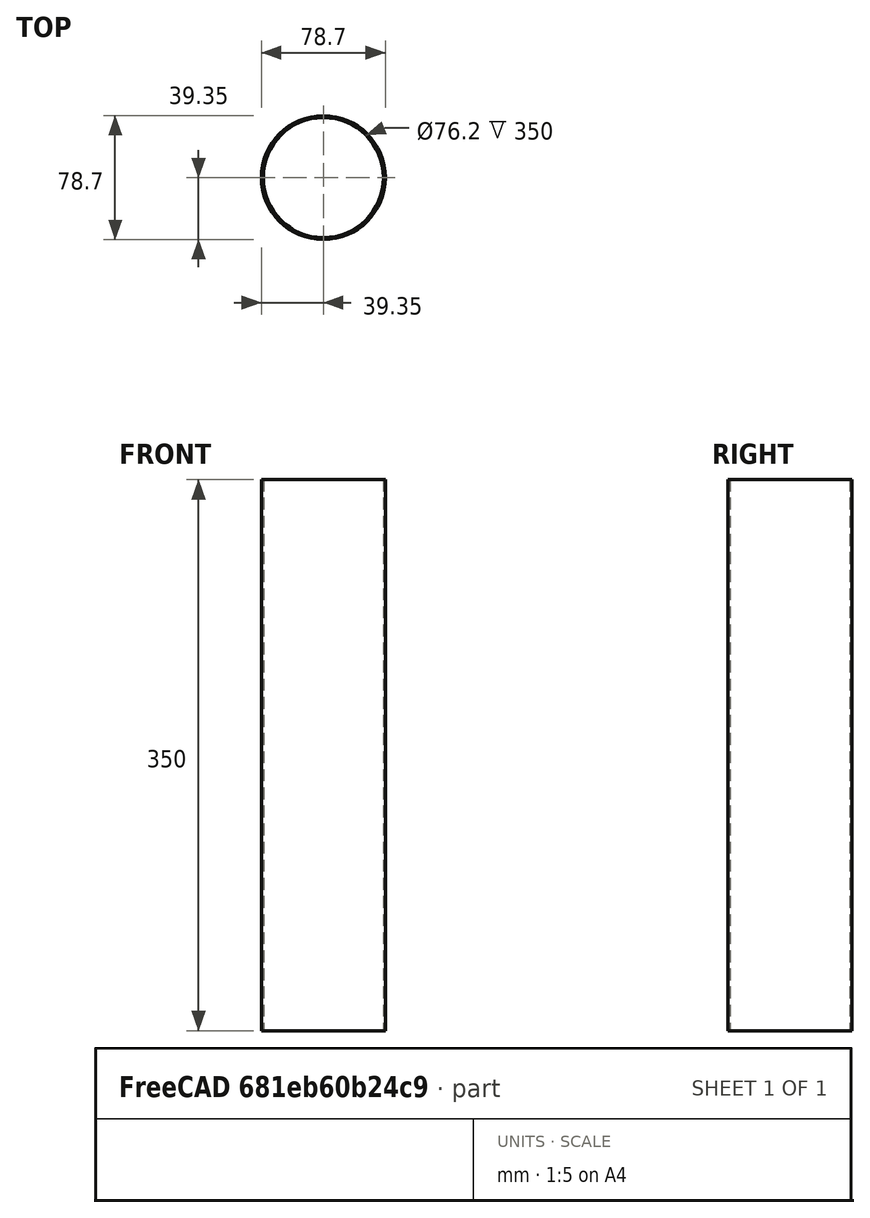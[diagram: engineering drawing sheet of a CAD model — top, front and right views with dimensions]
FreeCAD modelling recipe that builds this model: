
FCSTD DOCUMENT  (FreeCAD 1.0R39285 (Git))
Label: Bodytube
License: All rights reserved
LicenseURL: https://en.wikipedia.org/wiki/All_rights_reserved
objects: Sketcher::SketchObject×1, PartDesign::Pad×1, PartDesign::Hole×1, PartDesign::Body×1
note: 9 computed .brp shape members not serialized (recipe doc carries the construction recipe); baked Part::Feature solids carry a one-line shape summary decoded from their .brp

FEATURE [Sketcher::SketchObject] Sketch
  ArcFitTolerance = 1e-06
  AttachmentSupport = -> [XY_Plane]
  FullyConstrained = true
  MakeInternals = false
  MapMode = 5
  sketch-geometry (1):
    g0: Circle CenterX=0 CenterY=0 CenterZ=0 NormalX=0 NormalY=0 NormalZ=1 AngleXU=0 Radius=39.35
  constraints (2):
    c: Diameter(g0) = 78.7
    c: Coincident(g0,g-1)
FEATURE [PartDesign::Pad] Pad
  Direction = (0,0,1)
  Length = 350
  Length2 = 10
  Profile = -> Sketch
  ReferenceAxis = -> Sketch [N_Axis]
  Refine = true
  Suppressed = false
  Type = 0
FEATURE [PartDesign::Hole] Hole
  BaseFeature = -> Pad
  CustomThreadClearance = 0
  Depth = 741.741
  DepthType = 1
  Diameter = 76.2
  DrillForDepth = false
  DrillPoint = 1
  DrillPointAngle = 118
  HoleCutCountersinkAngle = 90
  HoleCutCustomValues = false
  HoleCutDepth = 0
  HoleCutDiameter = 6.1
  HoleCutType = 0
  ModelThread = false
  Profile = -> Pad [Face3]
  Refine = true
  Suppressed = false
  Tapered = false
  TaperedAngle = 90
  ThreadClass = 0
  ThreadDepth = 741.741
  ThreadDepthType = 0
  ThreadDirection = 0
  ThreadFit = 0
  ThreadSize = 0
  ThreadType = 0
  Threaded = false
  UseCustomThreadClearance = false
FEATURE [PartDesign::Body] Body
  AllowCompound = false
  Group = -> [Sketch,Pad,Hole]
  Origin = -> Origin
  Tip = -> Hole
